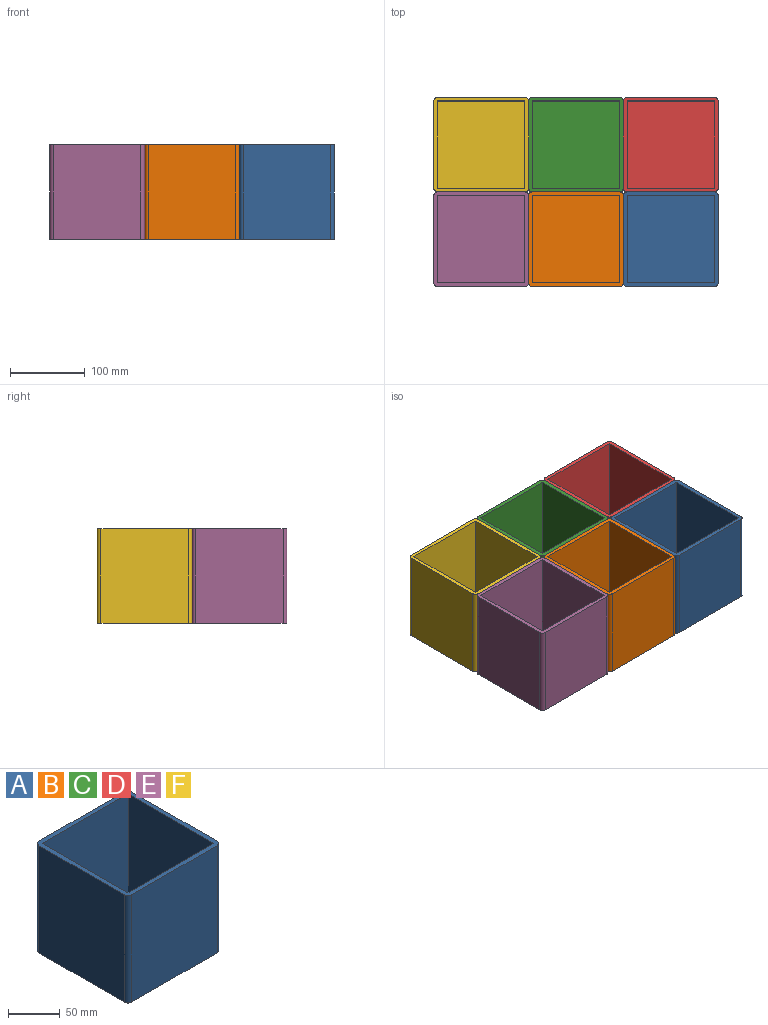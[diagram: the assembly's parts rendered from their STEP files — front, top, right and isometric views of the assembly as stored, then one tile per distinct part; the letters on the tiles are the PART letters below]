
ASSEMBLY  parts=6 mates=5
PART A: 15 faces, bbox 127x127x127 mm
  f0: plane 127x127mm, normal (0,0,1), area 2455.3mm2, adj f2,f3,f4,f5,f7,f8,f9,f10
  f1: plane 127x127mm, normal (0,0,-1), area 16106.8mm2, adj f2,f3,f4,f5,f11,f12,f13,f14
  f2: plane 127x116.84mm, normal (1,0,0), area 14838.7mm2, adj f0,f1,f11,f14
  f3: plane 127x116.84mm, normal (-1,0,0), area 14838.7mm2, adj f0,f1,f12,f13
  f4: plane 127x116.84mm, normal (0,-1,0), area 14838.7mm2, adj f0,f1,f11,f12
  f5: plane 127x116.84mm, normal (0,1,0), area 14838.7mm2, adj f0,f1,f13,f14
  f6: plane 116.84x116.84mm, normal (0,0,1), area 13651.6mm2, adj f7,f8,f9,f10
  f7: plane 121.92x116.84mm, normal (-1,0,0), area 14245.1mm2, adj f0,f6,f9,f10
  f8: plane 121.92x116.84mm, normal (1,0,0), area 14245.1mm2, adj f0,f6,f9,f10
  f9: plane 121.92x116.84mm, normal (0,1,0), area 14245.1mm2, adj f0,f6,f7,f8
  f10: plane 121.92x116.84mm, normal (0,-1,0), area 14245.1mm2, adj f0,f6,f7,f8
  f11: cylinder r=5.08mm len=127mm, axis (0,0,-1), area 1013.4mm2, adj f0,f1,f2,f4
  f12: cylinder r=5.08mm len=127mm, axis (0,0,1), area 1013.4mm2, adj f0,f1,f3,f4
  f13: cylinder r=5.08mm len=127mm, axis (0,0,-1), area 1013.4mm2, adj f0,f1,f3,f5
  f14: cylinder r=5.08mm len=127mm, axis (0,0,1), area 1013.4mm2, adj f0,f1,f2,f5
PART B: same geometry as A
PART C: same geometry as A
PART D: same geometry as A
PART E: same geometry as A
PART F: same geometry as A
PLACE A t=(-44.96,197.45,-44.6)mm
PLACE B t=(-171.96,197.45,-44.6)mm
PLACE C t=(-171.96,324.45,-44.6)mm
PLACE D t=(-44.96,324.45,-44.6)mm
PLACE E t=(-298.96,197.45,-44.6)mm
PLACE F t=(-298.96,324.45,-44.6)mm
MATE planar D.f4 <-> A.f5  axis (0,-1,0) through (-108.46,197.45,18.9)mm
MATE planar B.f2 <-> A.f3  axis (1,0,0) through (-171.96,133.95,18.9)mm
MATE planar E.f2 <-> B.f3  axis (1,0,0) through (-298.96,133.95,18.9)mm
MATE planar F.f4 <-> E.f5  axis (0,-1,0) through (-362.46,197.45,18.9)mm
MATE planar C.f4 <-> B.f5  axis (0,-1,0) through (-235.46,197.45,18.9)mm
